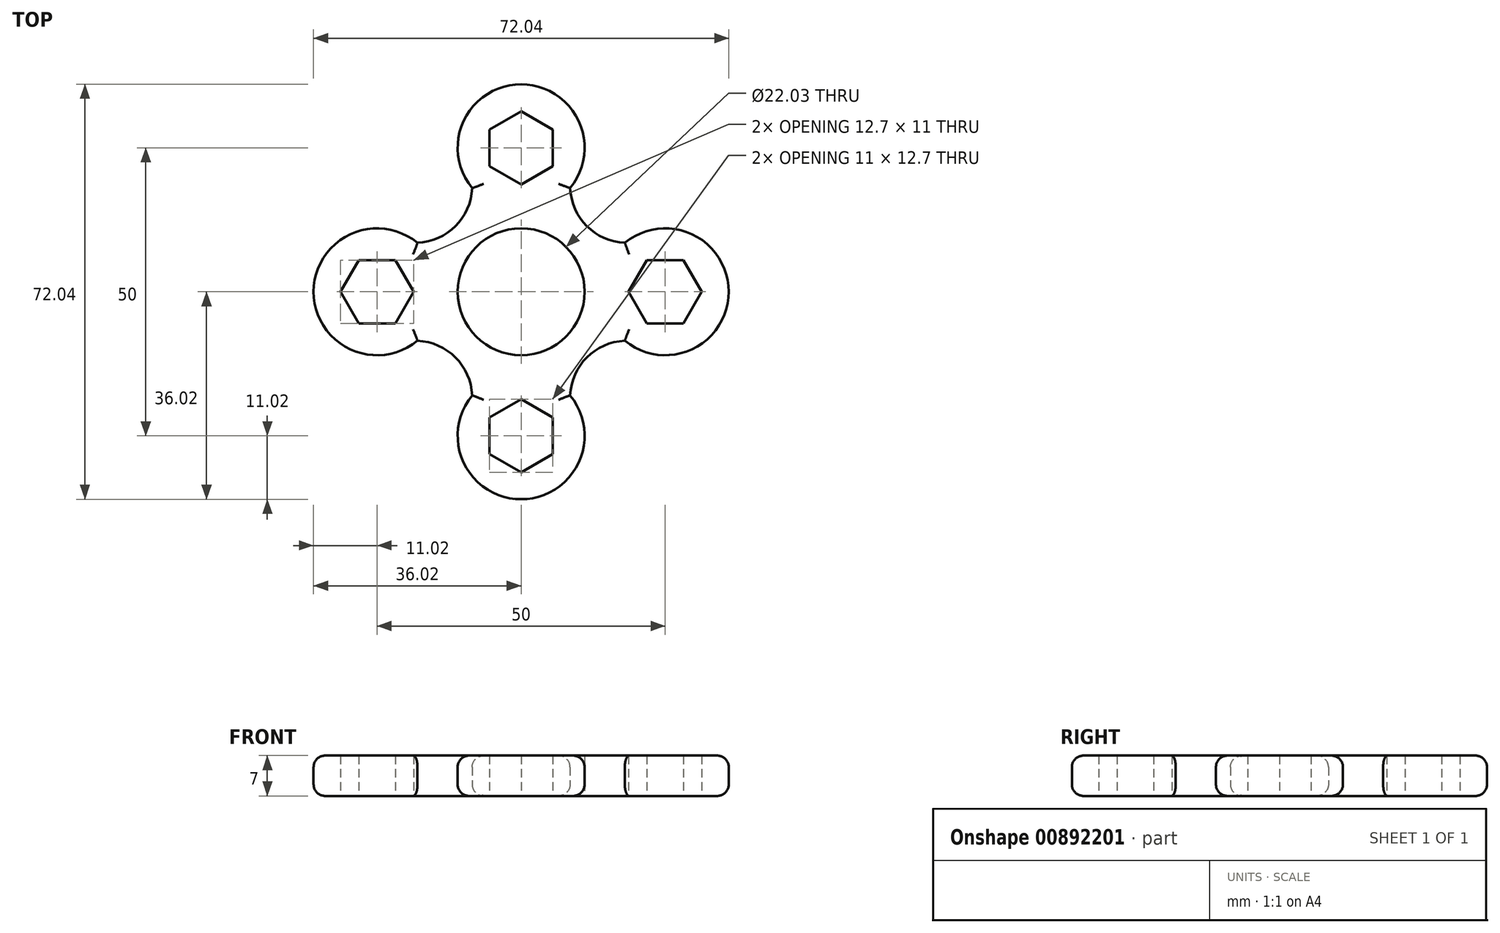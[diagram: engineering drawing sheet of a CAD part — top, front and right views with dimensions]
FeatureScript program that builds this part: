
annotation { "Feature Type Name" : "Feature", "Feature Type Description" : "" }
export const myFeature = defineFeature(function(context is Context, id is Id, definition is map)
    precondition{}
    {
        {
            var Q0;
            Q0=qCreatedBy(makeId("Top.planeOp"),FACE);
            var sketch = newSketch(context, id + "F0", { "sketchPlane" : qUnion([Q0])});
            skCircle(sketch, "E0", {"center": v(0, 0) * mm, "radius": 11.02 * mm});
            skArc(sketch, "E1", {"start": v(8.5, 18) * mm, "mid": v(0, 36.02) * mm, "end": v(-8.5, 18) * mm});
            skArc(sketch, "E2.1.0", {"start": v(-18, 8.5) * mm, "mid": v(-36.02, 0) * mm, "end": v(-18, -8.5) * mm});
            skArc(sketch, "E2.2.0", {"start": v(-8.5, -18) * mm, "mid": v(0, -36.02) * mm, "end": v(8.5, -18) * mm});
            skArc(sketch, "E2.3.0", {"start": v(18, -8.5) * mm, "mid": v(36.02, 0) * mm, "end": v(18, 8.5) * mm});
            skArc(sketch, "E3", {"start": v(-18, 8.5) * mm, "mid": v(-11.4, 11.4) * mm, "end": v(-8.5, 18) * mm});
            skArc(sketch, "E4.1.0", {"start": v(-8.5, -18) * mm, "mid": v(-11.4, -11.4) * mm, "end": v(-18, -8.5) * mm});
            skArc(sketch, "E4.2.0", {"start": v(18, -8.5) * mm, "mid": v(11.4, -11.4) * mm, "end": v(8.5, -18) * mm});
            skArc(sketch, "E4.3.0", {"start": v(8.5, 18) * mm, "mid": v(11.4, 11.4) * mm, "end": v(18, 8.5) * mm});
            skCircle(sketch, "E5.cCircle", {"center": v(0, 25) * mm, "radius": 5.5 * mm, "construction": true});
            skLineSegment(sketch, "E5.0", {"start": v(5.5, 28.18) * mm, "end": v(5.5, 21.82) * mm});
            skLineSegment(sketch, "E5.1", {"start": v(5.5, 21.82) * mm, "end": v(0, 18.65) * mm});
            skLineSegment(sketch, "E5.2", {"start": v(0, 18.65) * mm, "end": v(-5.5, 21.82) * mm});
            skLineSegment(sketch, "E5.3", {"start": v(-5.5, 21.82) * mm, "end": v(-5.5, 28.18) * mm});
            skLineSegment(sketch, "E5.4", {"start": v(-5.5, 28.18) * mm, "end": v(0, 31.35) * mm});
            skLineSegment(sketch, "E5.5", {"start": v(0, 31.35) * mm, "end": v(5.5, 28.18) * mm});
            skPoint(sketch, "E5.0.midPoint", {"position": v(5.5, 25) * mm});
            skLineSegment(sketch, "E6.1.0", {"start": v(-31.35, 0) * mm, "end": v(-28.18, 5.5) * mm});
            skLineSegment(sketch, "E6.1.1", {"start": v(-28.18, -5.5) * mm, "end": v(-31.35, 0) * mm});
            skLineSegment(sketch, "E6.1.2", {"start": v(-21.82, -5.5) * mm, "end": v(-28.18, -5.5) * mm});
            skLineSegment(sketch, "E6.1.3", {"start": v(-18.65, 0) * mm, "end": v(-21.82, -5.5) * mm});
            skLineSegment(sketch, "E6.1.4", {"start": v(-21.82, 5.5) * mm, "end": v(-18.65, 0) * mm});
            skLineSegment(sketch, "E6.1.5", {"start": v(-28.18, 5.5) * mm, "end": v(-21.82, 5.5) * mm});
            skLineSegment(sketch, "E6.2.0", {"start": v(0, -31.35) * mm, "end": v(-5.5, -28.18) * mm});
            skLineSegment(sketch, "E6.2.1", {"start": v(5.5, -28.18) * mm, "end": v(0, -31.35) * mm});
            skLineSegment(sketch, "E6.2.2", {"start": v(5.5, -21.82) * mm, "end": v(5.5, -28.18) * mm});
            skLineSegment(sketch, "E6.2.3", {"start": v(0, -18.65) * mm, "end": v(5.5, -21.82) * mm});
            skLineSegment(sketch, "E6.2.4", {"start": v(-5.5, -21.82) * mm, "end": v(0, -18.65) * mm});
            skLineSegment(sketch, "E6.2.5", {"start": v(-5.5, -28.18) * mm, "end": v(-5.5, -21.82) * mm});
            skLineSegment(sketch, "E6.3.0", {"start": v(31.35, 0) * mm, "end": v(28.18, -5.5) * mm});
            skLineSegment(sketch, "E6.3.1", {"start": v(28.18, 5.5) * mm, "end": v(31.35, 0) * mm});
            skLineSegment(sketch, "E6.3.2", {"start": v(21.82, 5.5) * mm, "end": v(28.18, 5.5) * mm});
            skLineSegment(sketch, "E6.3.3", {"start": v(18.65, 0) * mm, "end": v(21.82, 5.5) * mm});
            skLineSegment(sketch, "E6.3.4", {"start": v(21.82, -5.5) * mm, "end": v(18.65, 0) * mm});
            skLineSegment(sketch, "E6.3.5", {"start": v(28.18, -5.5) * mm, "end": v(21.82, -5.5) * mm});
            skSolve(sketch);
        }
        {
            var Q0;
            Q0 = qSketchRegion(id + "F0", true);
            extrude(context, id + "F1", {"entities" : qUnion([Q0]), "depth" : 7 * mm, "offsetDistance" : 25 * mm});
        }
        {
            var Q0;
            Q0=makeQuery(id+"F1.opExtrude","CAP_EDGE",EDGE,{"disambiguationData":[OSD([sQuery(id+"F0.wireOp",EDGE,"E4.3.0")])],"isStart":false});
            var Q1;
            Q1=makeQuery(id+"F1.opExtrude","CAP_EDGE",EDGE,{"disambiguationData":[OSD([sQuery(id+"F0.wireOp",EDGE,"E4.2.0")])],"isStart":false});
            var Q2;
            Q2=makeQuery(id+"F1.opExtrude","CAP_EDGE",EDGE,{"disambiguationData":[OSD([sQuery(id+"F0.wireOp",EDGE,"E4.1.0")])],"isStart":false});
            var Q3;
            Q3=makeQuery(id+"F1.opExtrude","CAP_EDGE",EDGE,{"disambiguationData":[OSD([sQuery(id+"F0.wireOp",EDGE,"E3")])],"isStart":false});
            var Q4;
            Q4=makeQuery(id+"F1.opExtrude","CAP_EDGE",EDGE,{"disambiguationData":[OSD([sQuery(id+"F0.wireOp",EDGE,"E1")])],"isStart":false});
            var Q5;
            Q5=makeQuery(id+"F1.opExtrude","CAP_EDGE",EDGE,{"disambiguationData":[OSD([sQuery(id+"F0.wireOp",EDGE,"E2.3.0")])],"isStart":false});
            var Q6;
            Q6=makeQuery(id+"F1.opExtrude","CAP_EDGE",EDGE,{"disambiguationData":[OSD([sQuery(id+"F0.wireOp",EDGE,"E2.2.0")])],"isStart":false});
            var Q7;
            Q7=makeQuery(id+"F1.opExtrude","CAP_EDGE",EDGE,{"disambiguationData":[OSD([sQuery(id+"F0.wireOp",EDGE,"E2.1.0")])],"isStart":false});
            fillet(context, id + "F2", {"entities" : qUnion([Q0, Q1, Q2, Q3, Q4, Q5, Q6, Q7]), "radius" : 2 * mm, "tangentPropagation" : true, "allowEdgeOverflow" : false});
        }
        {
            var Q0;
            Q0=makeQuery(id+"F1.opExtrude","CAP_EDGE",EDGE,{"disambiguationData":[OSD([sQuery(id+"F0.wireOp",EDGE,"E3")])],"isStart":true});
            var Q1;
            Q1=makeQuery(id+"F1.opExtrude","CAP_EDGE",EDGE,{"disambiguationData":[OSD([sQuery(id+"F0.wireOp",EDGE,"E4.3.0")])],"isStart":true});
            var Q2;
            Q2=makeQuery(id+"F1.opExtrude","CAP_EDGE",EDGE,{"disambiguationData":[OSD([sQuery(id+"F0.wireOp",EDGE,"E4.2.0")])],"isStart":true});
            var Q3;
            Q3=makeQuery(id+"F1.opExtrude","CAP_EDGE",EDGE,{"disambiguationData":[OSD([sQuery(id+"F0.wireOp",EDGE,"E4.1.0")])],"isStart":true});
            var Q4;
            Q4=makeQuery(id+"F1.opExtrude","CAP_EDGE",EDGE,{"disambiguationData":[OSD([sQuery(id+"F0.wireOp",EDGE,"E2.3.0")])],"isStart":true});
            var Q5;
            Q5=makeQuery(id+"F1.opExtrude","CAP_EDGE",EDGE,{"disambiguationData":[OSD([sQuery(id+"F0.wireOp",EDGE,"E2.2.0")])],"isStart":true});
            var Q6;
            Q6=makeQuery(id+"F1.opExtrude","CAP_EDGE",EDGE,{"disambiguationData":[OSD([sQuery(id+"F0.wireOp",EDGE,"E2.1.0")])],"isStart":true});
            var Q7;
            Q7=makeQuery(id+"F1.opExtrude","CAP_EDGE",EDGE,{"disambiguationData":[OSD([sQuery(id+"F0.wireOp",EDGE,"E1")])],"isStart":true});
            fillet(context, id + "F3", {"entities" : qUnion([Q0, Q1, Q2, Q3, Q4, Q5, Q6, Q7]), "radius" : 2 * mm, "tangentPropagation" : true, "allowEdgeOverflow" : false});
        }
        {
            var Q0;
            Q0=makeQuery(id+"F1.opExtrude","CAP_EDGE",EDGE,{"disambiguationData":[OSD([sQuery(id+"F0.wireOp",EDGE,"E0")])],"isStart":true});
            var Q1;
            Q1=makeQuery(id+"F1.opExtrude","CAP_EDGE",EDGE,{"disambiguationData":[OSD([sQuery(id+"F0.wireOp",EDGE,"E0")])],"isStart":false});
            fillet(context, id + "F4", {"entities" : qUnion([Q0, Q1]), "radius" : 0.02 * mm, "tangentPropagation" : true, "allowEdgeOverflow" : false});
        }
    });
